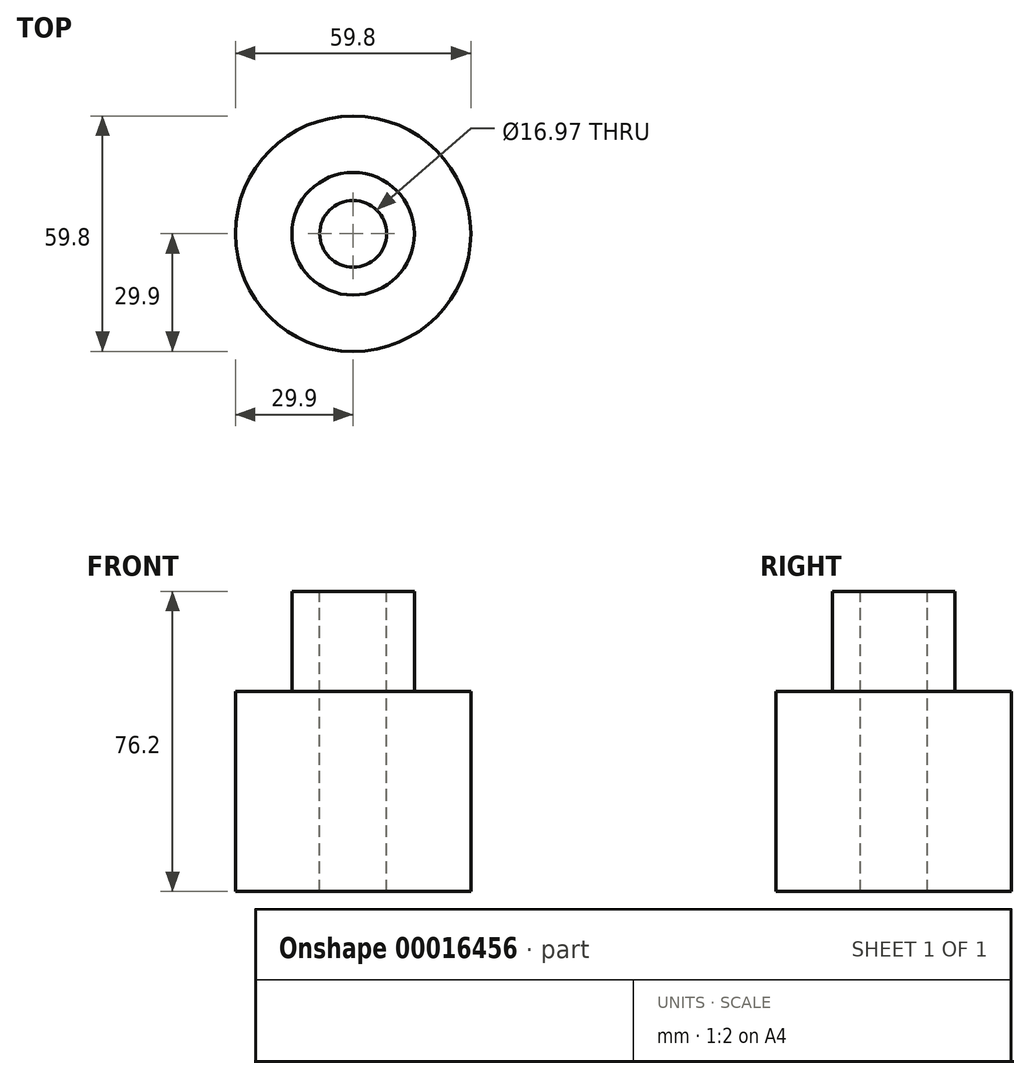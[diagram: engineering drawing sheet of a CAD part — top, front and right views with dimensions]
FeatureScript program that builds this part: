
annotation { "Feature Type Name" : "Feature", "Feature Type Description" : "" }
export const myFeature = defineFeature(function(context is Context, id is Id, definition is map)
    precondition{}
    {
        {
            var Q0;
            Q0=qCreatedBy(makeId("Top.planeOp"),FACE);
            var sketch = newSketch(context, id + "F0", { "sketchPlane" : qUnion([Q0])});
            skCircle(sketch, "E0", {"center": v(0, 0) * mm, "radius": 29.9 * mm});
            skSolve(sketch);
        }
        {
            var Q0;
            Q0 = qSketchRegion(id + "F0", true);
            extrude(context, id + "F1", {"entities" : qUnion([Q0]), "depth" : 25.4 * mm});
        }
        {
            var Q0;
            Q0=makeQuery(id+"F1.opExtrude","CAP_FACE",FACE,{"disambiguationData":[OSD([sQuery(id+"F0.wireOp",EDGE,"E0")])],"isStart":false});
            extrude(context, id + "F2", {"entities" : qUnion([Q0]), "operationType" : NewBodyOperationType.ADD, "depth" : 25.4 * mm});
        }
        {
            var Q0;
            Q0=makeQuery(id+"F2.opExtrude","CAP_FACE",FACE,{"disambiguationData":[OSD([sQuery(id+"F0.wireOp",EDGE,"E0")])],"isStart":false});
            var sketch = newSketch(context, id + "F3", { "sketchPlane" : qUnion([Q0])});
            skCircle(sketch, "E1", {"center": v(0, 0) * mm, "radius": 15.57 * mm});
            skSolve(sketch);
        }
        {
            var Q0;
            Q0 = qSketchRegion(id + "F3", true);
            extrude(context, id + "F4", {"entities" : qUnion([Q0]), "operationType" : NewBodyOperationType.ADD, "depth" : 25.4 * mm});
        }
        {
            var Q0;
            Q0=makeQuery(id+"F4.opExtrude","CAP_FACE",FACE,{"disambiguationData":[OSD([sQuery(id+"F3.wireOp",EDGE,"E1")])],"isStart":false});
            var sketch = newSketch(context, id + "F5", { "sketchPlane" : qUnion([Q0])});
            skCircle(sketch, "E2", {"center": v(0, 0) * mm, "radius": 8.49 * mm});
            skSolve(sketch);
        }
        {
            var Q0;
            Q0=makeQuery(id+"F5.imprint","IMPRINT",FACE,{"disambiguationData":[TD([[makeQuery(id+"F5.imprint","IMPRINT",EDGE,{"derivedFrom":sQuery(id+"F5.wireOp",EDGE,"E2")}),1.0]])]});
            extrude(context, id + "F6", {"entities" : qUnion([Q0]), "operationType" : NewBodyOperationType.REMOVE, "endBound" : BoundingType.THROUGH_ALL, "oppositeDirection" : true, "depth" : 25.4 * mm});
        }
    });
